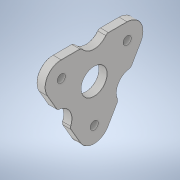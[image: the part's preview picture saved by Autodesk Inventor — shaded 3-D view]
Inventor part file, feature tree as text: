
AUTODESK INVENTOR PART (.ipt)
format: ipt  version: 2021 (Build 250183000, 183)  size: 241,152 bytes
history: native  units: in
note: dims shown in document units (in); Inventor stores cm internally (conversion verified against a paired STEP export)
features: extrude x2, sketch x2, fillet x1, chamfer x1
ambient origin geometry x8: Origin, YZ Plane, XZ Plane, XY Plane, X Axis, Y Axis, Z Axis, Center Point
bodies: Solid1 (feature_tree)
feature tree (6):
  extrude  "Extrusion1"  Depth=0.125in TaperAngle=360.0deg
  fillet  "Fillet2"  Radius=0.125in
  extrude  "Extrusion3"  Depth=0.125in
  chamfer  "Chamfer4"  Distance=0.3153in
  sketch  "Sketch1"  dims[d4=0.325in d5=0.0in d26=1.1811in d28=360.0deg d30=0.125in]
  sketch  "Sketch5"  dims[d34=1.25in d35=1.135in d36=0.3153in d37=1.25in d38=1.25in d39=60.0deg d40=60.0deg d41=0.2903in d42=2.1897in d43=2.1897in d44=0.0in d45=1.6222in d46=0.0in d47=2.4668in d48=3.1515in d49=0.0in d50=3.1515in d51=0.625in d52=0.625in d53=0.9375in d54=3.1515in d55=1.363in d56=1.363in d57=1.6222in d58=0.0in d59=1.6222in d60=2.4668in d61=2.4668in d62=0.0in d63=2.4668in d64=1.6222in d65=2.839in d66=3.1515in d67=0.0in d68=3.1515in d69=0.9375in d70=1.0in d71=1.0in d72=0.0in d73=0.01in d74=0.125in d75=45.0deg]
